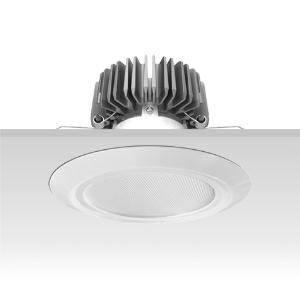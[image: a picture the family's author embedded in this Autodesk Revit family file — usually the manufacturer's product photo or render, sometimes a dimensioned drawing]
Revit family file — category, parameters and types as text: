
# Revit family: 3f_filippi_-_3f_reno_bianco_ampio_3f_filippi_-_30675_a01048_-_3f_reno_200_wh_2000-930_dali_wide___smp_wh_e2cf
name_source: partatom
category: Lighting Fixtures
units: mm (PartAtom-declared; Revit-internal decimal feet)

## family parameters
Cut with Voids When Loaded = No
Host = Face
Light Source = No
Part Type = Normal
Room Calculation Point = No
Round Connector Dimension = Use Diameter
Shared = No

## types (1)
- 3F Filippi - 3F Reno Bianco Ampio (1 x LED, 1650 lm, 24 W, 3000 K)
    Apparent Load = 24 VA
    Approval mark = CE
    CIE Flux Codes = 74 92 98 100 100
    Color Rendering = 90
    Color Temperature = 3000 K
    Control Gear = Electronic transformer
    Default Elevation = 1800 mm
    Description = ILLUMINOTECHNICAL
Luminous efficiency 100% (DLOR 100%, ULOR 0%).
Initial luminous flux of the luminaire 1650 lm.
Direct symmetric wide distribution.
Installation Interdistance Transv.D = 1.06 x hu - Long.D = 1.04 x hu.
Average luminance <3000 cd/m² for radial angles >65°.
Tabular UGR (CIE 117 - 4H-8H; S=0.25H; 70/50/20): RUG 21.3 - 21.1.
Beam angle: 70° - 69°.
Luminous efficacy 69 lm/W.
Lifetime (L90/B10): 30000 h. (tq+25°C)
Lifetime (L85/B10): 50000 h. (tq+25°C)
Lifetime (L70/B10): 80000 h. (tq+25°C)
Sudden decreased luminous flux after 50000 hours: 0% (C0).
Photobiological safety in compliance with IEC/TR 62778: RG0 risk exempt, (IEC 62471).
In compliance with IEC/EN 62722-2-1 - IEC/EN 62717 standards.

SOURCE
Compact LED module 2000/930.
Energy efficiency class (UE 2019/2020 - UE 2019/2015): E.
CIE 13.3 Colour rendering index: CRI >90 (R9 >50%).
IES TM-30 Fidelity Index: Rf = 92 Rg = 101.
CCT nominal colour temperature 3000 K.
Colour initial tolerance (MacAdam): SDCM 3.
Zhaga Book 3 compliant.

MECHANICAL
Passive heat dissipator in die-casting aluminium, oversized, for optimum thermal management of the LED module.
Parabolic element with graduated/concentric rings in white polycarbonate.
Transparent external lens with glossy and satin differentiated surfaces, with a cooling and anti-insect system in methacrylate (PMMA).
Fastening spring clips in stainless steel.
Dimensions: diameter 226 mm, height 146 mm. Weight 1.04 kg.
IP44 protection degree for exposed part, IP20 for recessed part.
Mechanical strength to impacts IK05 (0.7 joule).
Glow-wire test resistance 650°C.

ELECTRICAL
Wiring on a separate unit.
Halogen Free DALI-2 DATI (Parts 251, 252, 253), PUSH-DIM, electronic wiring 230V-50/60Hz, power factor 0.95 at full load, THD <25%, constant output current, SELV, class II, 1 driver, 1 DALI addresse.
Power of the luminaire 24 W.
ENEC - CE.
SAFE FLICKER: PstLM=<1 and SVM=<0.4 (IEC TR 61547-1 and IEC TR 63158), to ensure a more comfortable and safe light.
Luminaire compliant with EN 60598-2-22 for power supply from a centralised emergency system CPSS (Central Power Supply System), not incorporated in the luminaire - high risk areas excluded. The default power and flux are 100% in AC and 100% in DC.
Ambient temperature from 0°C to +25°C.
Temperature class T6 max 85°C.
Relative humidity UR: <85%.

INSTALLATION
Pull-up recessed fitting.
False ceiling carving: 200 mm.
All accessories dedicated to this product are available on the Catalog and on our website www.3F-Filippi.com.

ACCESSORIES
A01048 - Anti-glare microprismatic SMP diffuser in methacrylate (PMMA), locked and in line with the trim, in white polycarbonate.

APPLICATIONS
Suitable product for food production plants (HACCP), IFS (Food Version 6), BRC (GSFS Food Version 7).
Environments: architectural, commercial, exhibition areas, transit areas, corridors, shops, display windows, service areas.
In false ceilings with narrow voids.

LIGHT MANAGEMENT
Recommended minimum setting: 10%.
The luminaire, equipped with (DALI-2 DATI) driver, can be controlled manually with 3F Easy Dim technology or automatically/manually with wired or wireless DALI/D2D control systems.
The D2D driver guarantees interoperability with other devices with the same certification by making the following information available:
Device Data (Part 251), Energy Report (Part 252), Diagnosis & Maintenance (Part 253).
In electrical systems without a regulation system (manual or automatic) and DALI bus, a suitable jumper must be made on the DA-DA terminals of the appliance.

WARNING
Luminaire designed for disposal/recycling at end-of-life.
Replaceable (LED only) light source by a professional. Replaceable control gear by a professional.
    Height = 0 mm  [stored 0 ft]
    Lamp = 1 x LED
    Lamp Light Flux = 1650 lm
    Lamp Power = 24 W
    Lamp count = 1
    Length = 226 mm
    Lifetime = 50000 h
    Luminous efficacy = 69 lm/W
    Manufacturer = 3F Filippi
    ModVariant = No
    Model = 3F Filippi - 30675+A01048 - 3F Reno 200 WH 2000-930 DALI WIDE + SMP WH
    Mounting Place = Ceiling
    Mounting Type = Recessed
    Number of Poles = 1
    OnlyDefault = Yes
    Power Factor = 1
    Product Name = 3F Filippi - 3F Reno Bianco Ampio
    Product group = recessed luminaire
    ProductGroupID = 4
    Protection Class = Protection class II
    Protection Degree = IP 20
    RLX_Detail_Level = 1
    RLX_Emergency_Light_Flux = 0 lm
    RLX_Emergency_Type = 0
    RLX_Emergency_Type_DB = No
    RlxData = <blob elided: 97317 chars, md5=6bb2c676>
    Socket = socket
    Standby Power = 0 W
    System Light Flux = 1650 lm
    System Power = 24 W
    Type Comments = Product without accessories
    Type Image = 3ffilippi_3f_reno_200_wh_vs_smp.jpg
    URL = http://relux.com
    VarID = ---
    Voltage = 0 V
    Weight = 0.00 kg
    Width = 0 mm  [stored 0 ft]

note: [stored X ft] marks values corroborated as IEEE doubles in the binary element streams (Revit-internal decimal feet)

## geometry (parser evidence)
native form markers: Blend x4, Sweep x11
no freeform markers — native parametric forms only
